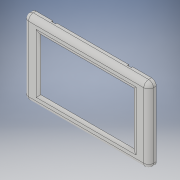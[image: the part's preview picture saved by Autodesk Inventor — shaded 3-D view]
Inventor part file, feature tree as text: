
AUTODESK INVENTOR PART (.ipt)
format: ipt  version: 2018 (Build 220112000, 112)  size: 264,704 bytes
history: native  units: in
note: dims shown in document units (in); Inventor stores cm internally (conversion verified against a paired STEP export)
features: extrude x9, sketch x9, fillet x3, shell x1
ambient origin geometry x8: Origin, YZ Plane, XZ Plane, XY Plane, X Axis, Y Axis, Z Axis, Center Point
bodies: Solid1 (feature_tree)
feature tree (22):
  extrude  "Extrusion1"  Depth=4.4094in
  shell  "Shell1"  Thickness=0.3898in
  fillet  "Fillet1"  Radius=0.25in
  extrude  "Extrusion2"  Depth=0.315in
  extrude  "Extrusion3"  Depth=0.25in TaperAngle=0.0deg
  extrude  "Extrusion4"  Depth=0.125in
  extrude  "Extrusion5"  Depth=0.0787in
  extrude  "Extrusion6"  Depth=0.0787in
  extrude  "Extrusion7"  Depth=0.0787in
  extrude  "Extrusion10"  Depth=0.2in TaperAngle=0.0deg
  extrude  "Extrusion11"  Depth=0.315in
  fillet  "Fillet6"  Radius=1.378in
  fillet  "Fillet7"  Radius=0.0492in
  sketch  "Sketch1"  dims[d0=7.6772in d1=4.4094in d2=0.3898in d3=0.0in d4=0.25in]
  sketch  "Sketch2"  dims[d5=0.315in d6=6.1024in]
  sketch  "Sketch3"  dims[d7=3.4252in d8=0.25in d9=0.0in]
  sketch  "Sketch4"  dims[d14=0.125in d15=0.0in d22=0.0787in]
  sketch  "Sketch5"  dims[d23=0.0787in d24=0.0787in]
  sketch  "Sketch6"  dims[d25=0.0787in d26=0.0787in]
  sketch  "Sketch7"  dims[d27=0.0787in d28=0.0787in]
  sketch  "Sketch9"  dims[d29=0.0787in d30=0.2in d31=0.0in]
  sketch  "Sketch10"  dims[d32=0.3346in d33=1.2598in d34=1.378in d35=0.0492in d36=0.2402in d37=0.0in d38=0.0492in d39=0.2402in d40=0.0in d41=1.0in d42=0.0in d43=0.097in d44=0.0in d47=0.2559in d48=0.2559in d49=0.0866in d50=0.0in d57=4.9606in d58=1.2894in d69=0.1181in d70=0.1181in d71=0.1181in d72=0.1181in d73=0.1181in d74=0.0in d75=0.0394in d76=0.0in d77=0.315in d78=0.315in]
